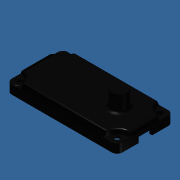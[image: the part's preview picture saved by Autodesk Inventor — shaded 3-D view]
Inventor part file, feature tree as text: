
AUTODESK INVENTOR PART (.ipt)
format: ipt  version: 2014 (Build 180170000, 170)  size: 451,584 bytes
history: native  units: in
note: dims shown in document units (in); Inventor stores cm internally (conversion verified against a paired STEP export)
features: extrude x9, sketch x9, fillet x6, mirror x2, chamfer x2
ambient origin geometry x8: Origin, YZ Plane, XZ Plane, XY Plane, X Axis, Y Axis, Z Axis, Center Point
bodies: Solid1 (feature_tree), Solid2 (feature_tree)
feature tree (28):
  extrude  "Extrusion1"  Depth=1.6063in
  extrude  "Extrusion3"  Depth=0.1969in
  extrude  "Extrusion4"  Depth=0.0787in
  mirror  "Mirror2"
  mirror  "Mirror3"
  chamfer  "Chamfer1"  Distance=0.0709in
  chamfer  "Chamfer2"  Distance=0.0787in Angle=45.0deg
  fillet  "Fillet1"  Radius=0.0787in
  fillet  "Fillet2"  Radius=0.0197in
  extrude  "Extrusion5"  Depth=0.3937in
  fillet  "Fillet3"  Radius=0.2165in
  extrude  "Extrusion6"  Depth=0.0394in
  extrude  "Extrusion7"  Depth=0.0394in
  fillet  "Fillet4"  Radius=0.0394in
  fillet  "Fillet5"  Radius=0.0394in
  fillet  "Fillet6"  Radius=0.0394in
  extrude  "Extrusion8"  Depth=0.0906in TaperAngle=0.0deg
  extrude  "Extrusion9"  Depth=0.0591in TaperAngle=0.0deg
  extrude  "Extrusion10"  Depth=0.0039in
  sketch  "Sketch1"  dims[d0=1.6063in d1=0.8189in]
  sketch  "Sketch3"  dims[d2=0.1969in d3=0.0in d6=0.1969in]
  sketch  "Sketch4"  dims[d7=0.0709in d8=0.0in d9=0.0787in]
  sketch  "Sketch5"  dims[d12=0.0984in]
  sketch  "Sketch6"  dims[d13=0.0984in d14=0.0709in d15=0.0in d16=0.0787in d17=0.0394in d18=45.0deg]
  sketch  "Sketch7"  dims[d19=0.0787in d20=0.0394in d21=45.0deg d22=0.0787in d23=0.0197in]
  sketch  "Sketch8"  dims[d24=0.3937in d25=0.3937in d27=0.2165in]
  sketch  "Sketch9"  dims[d28=0.2362in d29=0.0in d30=0.0394in]
  sketch  "Sketch10"  dims[d31=0.0394in d32=0.0394in d33=0.0394in d34=0.0394in d35=0.0394in d36=0.0906in d37=0.0in d38=0.0591in d39=0.0in d40=0.0039in d41=0.0039in d42=0.0039in d43=0.1969in d44=0.0787in d45=0.0472in d46=0.0in d56=0.0709in d57=0.0709in d58=0.0787in d59=0.0787in d62=0.0in d63=0.2032in d64=0.0472in d65=0.0in d66=1.9685in d67=1.1811in d68=0.4656in d69=0.0in]
